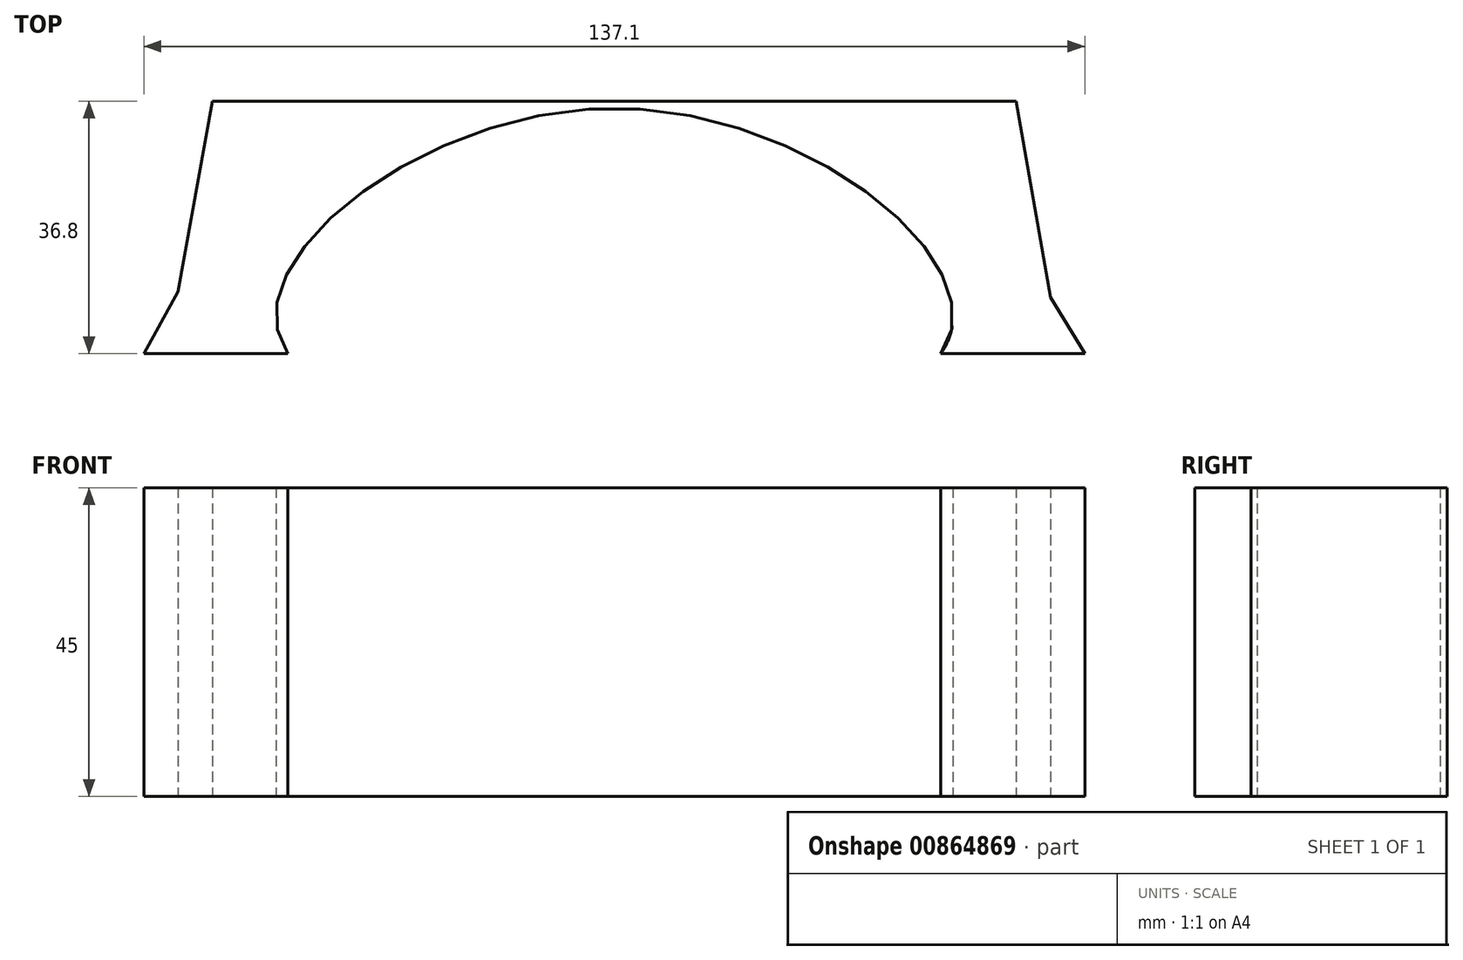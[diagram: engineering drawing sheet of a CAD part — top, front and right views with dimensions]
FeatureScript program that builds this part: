
annotation { "Feature Type Name" : "Feature", "Feature Type Description" : "" }
export const myFeature = defineFeature(function(context is Context, id is Id, definition is map)
    precondition{}
    {
        {
            var Q0;
            Q0=qCreatedBy(makeId("Top.planeOp"),FACE);
            var sketch = newSketch(context, id + "F0", { "sketchPlane" : qUnion([Q0])});
            skLineSegment(sketch, "E0.bottom", {"start": v(98.55, -49.27) * mm, "end": v(-93.62, -49.27) * mm});
            skLineSegment(sketch, "E0.top", {"start": v(98.55, 49.27) * mm, "end": v(-98.55, 49.27) * mm});
            skLineSegment(sketch, "E0.left", {"start": v(98.55, -49.27) * mm, "end": v(98.55, 49.27) * mm});
            skLineSegment(sketch, "E0.right", {"start": v(-98.55, -44.35) * mm, "end": v(-98.55, 49.27) * mm});
            skPoint(sketch, "E0.middle", {"position": v(0, 0) * mm});
            skLineSegment(sketch, "E1", {"start": v(-98.55, -44.35) * mm, "end": v(-98.55, -49.27) * mm});
            skLineSegment(sketch, "E2", {"start": v(-98.55, -49.27) * mm, "end": v(-93.62, -49.27) * mm});
            skLineSegment(sketch, "E3", {"start": v(-98.55, -12.47) * mm, "end": v(98.55, -12.47) * mm});
            skLineSegment(sketch, "E4", {"start": v(-68.55, -49.27) * mm, "end": v(-63.55, -40.2) * mm});
            skLineSegment(sketch, "E5", {"start": v(-63.55, -40.2) * mm, "end": v(-58.55, -12.47) * mm});
            skLineSegment(sketch, "E6", {"start": v(68.55, -49.27) * mm, "end": v(63.55, -41.05) * mm});
            skLineSegment(sketch, "E7", {"start": v(63.55, -41.05) * mm, "end": v(58.55, -12.47) * mm});
            skFitSpline(sketch, "E8", {"points": [v(-47.55, -49.27) * mm, v(0, -13.47) * mm, v(47.55, -49.27) * mm, v(-47.55, -49.27) * mm]});
            skSolve(sketch);
        }
        {
            var Q0;
            {var subQ0=sQuery(id+"F0.wireOp",EDGE,"E4");Q0=makeQuery(id+"F0.imprint","IMPRINT",FACE,{"disambiguationData":[TD([[makeQuery(id+"F0.imprint","IMPRINT",EDGE,{"derivedFrom":subQ0}),-1.0]])]});}
            extrude(context, id + "F1", {"entities" : qUnion([Q0]), "depth" : 45 * mm, "offsetDistance" : 25 * mm});
        }
    });
